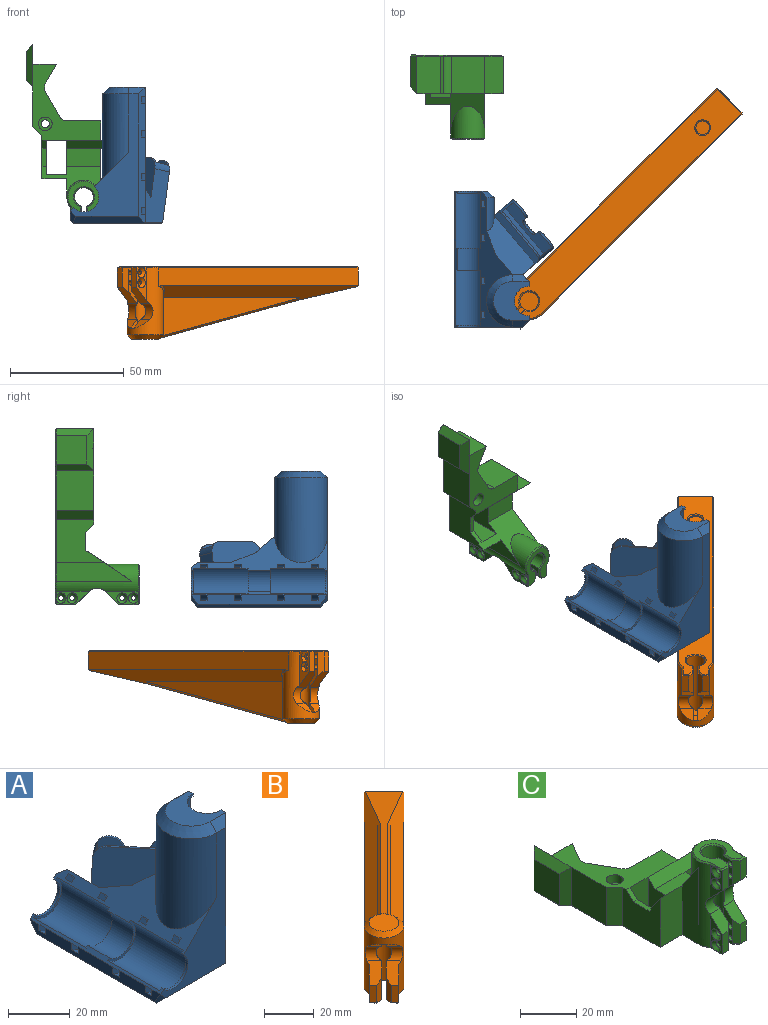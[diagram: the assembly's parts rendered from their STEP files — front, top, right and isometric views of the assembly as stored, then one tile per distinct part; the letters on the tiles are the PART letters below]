
ASSEMBLY  parts=3 mates=2
PART A: 114 faces, bbox 43.8x60x60 mm
  f0: plane 54x38.74mm, normal (0,0,-1), area 1335.7mm2, adj f1,f3,f13,f23,f24,f25,f27,f37
  f1: plane 16.85x14.14mm, normal (-0.77,-0.64,0), area 54.9mm2, adj f0,f98,f99,f100,f108,f109,f110
  f2: plane 22.93x19.76mm, normal (-0.75,-0.63,0.17), area 490.1mm2, adj f8,f81,f86,f92,f93,f94,f96
  f3: plane 11.55x8.31mm, normal (1,0,0), area 88.6mm2, adj f0,f9,f36,f81,f111
  f4: plane 24.28x21.91mm, normal (0.13,0.11,0.98), area 86.6mm2, adj f82,f83,f84,f88,f89,f90,f97
  f5: plane 60x15.09mm, normal (-0.71,0,0.71), area 433.6mm2, adj f9,f10,f11,f14,f15,f16,f17,f18
  f6: cylinder r=7.55mm len=24.1mm, axis (0,0,-1), area 571.6mm2, adj f23,f24,f31,f34
  f7: cylinder r=7.55mm len=24.1mm, axis (0,0,-1), area 571.6mm2, adj f23,f24,f28,f33
  f8: plane 0.26x0.16mm, normal (1,0,0), area 0mm2, adj f2,f9,f96
  f9: cylinder r=11.55mm len=14.54mm, axis (0,-1,0), area 110.4mm2, adj f3,f5,f8,f35,f96
  f10: cylinder r=7.55mm len=24.1mm, axis (0,-1,0), area 571.6mm2, adj f5,f12,f17,f21
  f11: cylinder r=7.55mm len=24.1mm, axis (0,-1,0), area 571.6mm2, adj f5,f12,f19,f22
  f12: plane 60x1.41mm, normal (-0.71,0,0.71), area 71.8mm2, adj f10,f11,f14,f15,f16,f17,f18,f19
  f13: plane 54x1.26mm, normal (-0.71,0,-0.71), area 96.3mm2, adj f0,f38,f39,f40
  f14: plane 14.6x14.6mm, normal (0,1,0), area 64.7mm2, adj f5,f12,f18,f35,f36,f37,f38
  f15: plane 54x30.05mm, normal (0,-1,0), area 557.1mm2, adj f5,f12,f16,f29,f40,f41,f42,f43
  f16: cylinder r=6.55mm len=11.18mm, axis (0,-1,0), area 20.6mm2, adj f5,f12,f15,f17
  f17: plane 12.89x12.89mm, normal (0,1,0), area 22.1mm2, adj f5,f10,f12,f16
  f18: cylinder r=6.55mm len=11.18mm, axis (0,1,0), area 20.6mm2, adj f5,f12,f14,f19
  f19: plane 12.89x12.89mm, normal (0,-1,0), area 22.1mm2, adj f5,f11,f12,f18
  f20: cylinder r=6.55mm len=11.18mm, axis (0,1,0), area 201.7mm2, adj f5,f12,f21,f22
  f21: plane 12.89x12.89mm, normal (0,-1,0), area 22.1mm2, adj f5,f10,f12,f20
  f22: plane 12.89x12.89mm, normal (0,1,0), area 22.1mm2, adj f5,f11,f12,f20
  f23: plane 60x2mm, normal (1,0,0), area 71.8mm2, adj f0,f6,f7,f26,f27,f28,f30,f31
  f24: plane 60x2mm, normal (1,0,0), area 71.8mm2, adj f0,f6,f7,f26,f27,f28,f30,f31
  f25: plane 57x4.28mm, normal (0,1,0), area 153.2mm2, adj f0,f29,f44,f46,f47,f86,f96,f113
  f26: plane 17.1x15.83mm, normal (0,0,1), area 172mm2, adj f23,f24,f30,f43,f45,f46
  f27: cylinder r=6.55mm len=13.1mm, axis (0,0,-1), area 20.6mm2, adj f0,f23,f24,f28
  f28: plane 15.1x7.55mm, normal (0,0,1), area 22.1mm2, adj f7,f23,f24,f27
  f29: cylinder r=11.55mm len=37.32mm, axis (0,0,1), area 1200.5mm2, adj f5,f15,f25,f45
  f30: cylinder r=6.55mm len=13.1mm, axis (0,0,1), area 20.6mm2, adj f23,f24,f26,f31
  f31: plane 15.1x7.55mm, normal (0,0,-1), area 22.1mm2, adj f6,f23,f24,f30
  f32: cylinder r=6.55mm len=13.1mm, axis (0,0,1), area 201.7mm2, adj f23,f24,f33,f34
  f33: plane 15.1x7.55mm, normal (0,0,-1), area 22.1mm2, adj f7,f23,f24,f32
  f34: plane 15.1x7.55mm, normal (0,0,1), area 22.1mm2, adj f6,f23,f24,f32
  f35: cone r=11.55mm half-angle=45deg, axis (0,-1,0), area 33.5mm2, adj f5,f9,f14,f36
  f36: plane 11.55x3mm, normal (0.71,0.71,0), area 42.6mm2, adj f3,f14,f35,f37
  f37: plane 16.33x3mm, normal (0,0.71,-0.71), area 60.3mm2, adj f0,f14,f36,f38
  f38: plane 5.5x3mm, normal (-0.5,0.71,-0.5), area 11.3mm2, adj f13,f14,f37,f39
  f39: plane 60x4.24mm, normal (-1,0,0), area 210.6mm2, adj f12,f13,f38,f40,f48,f49,f51,f52
  f40: plane 5.5x3mm, normal (-0.5,-0.71,-0.5), area 11.3mm2, adj f13,f15,f39,f41
  f41: plane 31.78x3mm, normal (0,-0.71,-0.71), area 125.8mm2, adj f0,f15,f40,f42
  f42: plane 60x3mm, normal (0.71,-0.71,0), area 210.6mm2, adj f15,f23,f41,f43,f65,f66,f67,f69
  f43: plane 7.28x3mm, normal (0,-0.71,0.71), area 24.5mm2, adj f15,f26,f42,f45
  f44: plane 60x3mm, normal (0.71,0.71,0), area 217mm2, adj f0,f24,f25,f46,f65,f66,f67,f69
  f45: cone r=8.55mm half-angle=45deg, axis (0,0,-1), area 134mm2, adj f26,f29,f43,f46
  f46: plane 7.28x3mm, normal (0,0.71,0.71), area 24.5mm2, adj f25,f26,f44,f45
  f47: plane 8.66x7.27mm, normal (0.77,0.64,0), area 41.1mm2, adj f5,f25,f96
  f48: cylinder r=10.55mm len=18.01mm, axis (0,-1,0), area 93.9mm2, adj f5,f39,f49,f51
  f49: plane 18.01x16.6mm, normal (0,-1,0), area 58.1mm2, adj f5,f39,f48,f50
  f50: cylinder r=8.55mm len=14.6mm, axis (0,-1,0), area 80.6mm2, adj f5,f12,f49,f51
  f51: plane 18.01x16.6mm, normal (0,1,0), area 58.1mm2, adj f5,f39,f48,f50
  f52: cylinder r=10.55mm len=18.01mm, axis (0,-1,0), area 93.9mm2, adj f5,f39,f53,f55
  f53: plane 18.01x16.6mm, normal (0,-1,0), area 58.1mm2, adj f5,f39,f52,f54
  f54: cylinder r=8.55mm len=14.6mm, axis (0,-1,0), area 80.6mm2, adj f5,f12,f53,f55
  f55: plane 18.01x16.6mm, normal (0,1,0), area 58.1mm2, adj f5,f39,f52,f54
  f56: cylinder r=10.55mm len=18.01mm, axis (0,1,0), area 93.9mm2, adj f5,f39,f57,f59
  f57: plane 18.01x16.6mm, normal (0,1,0), area 58.1mm2, adj f5,f39,f56,f58
  f58: cylinder r=8.55mm len=14.6mm, axis (0,1,0), area 80.6mm2, adj f5,f12,f57,f59
  f59: plane 18.01x16.6mm, normal (0,-1,0), area 58.1mm2, adj f5,f39,f56,f58
  f60: cylinder r=10.55mm len=18.01mm, axis (0,1,0), area 93.9mm2, adj f5,f39,f61,f63
  f61: plane 18.01x16.6mm, normal (0,1,0), area 58.1mm2, adj f5,f39,f60,f62
  f62: cylinder r=8.55mm len=14.6mm, axis (0,1,0), area 80.6mm2, adj f5,f12,f61,f63
  f63: plane 18.01x16.6mm, normal (0,-1,0), area 58.1mm2, adj f5,f39,f60,f62
  f64: cylinder r=8.55mm len=17.1mm, axis (0,0,1), area 80.6mm2, adj f23,f24,f65,f67
  f65: plane 20.78x10.55mm, normal (0,0,-1), area 56.2mm2, adj f42,f44,f64,f66
  f66: cylinder r=10.55mm len=20.78mm, axis (0,0,1), area 88.3mm2, adj f42,f44,f65,f67
  f67: plane 20.78x10.55mm, normal (0,0,1), area 56.2mm2, adj f42,f44,f64,f66
  f68: cylinder r=8.55mm len=17.1mm, axis (0,0,1), area 80.6mm2, adj f23,f24,f69,f71
  f69: plane 20.78x10.55mm, normal (0,0,-1), area 56.2mm2, adj f42,f44,f68,f70
  f70: cylinder r=10.55mm len=20.78mm, axis (0,0,1), area 88.3mm2, adj f42,f44,f69,f71
  f71: plane 20.78x10.55mm, normal (0,0,1), area 56.2mm2, adj f42,f44,f68,f70
  f72: cylinder r=8.55mm len=17.1mm, axis (0,0,-1), area 80.6mm2, adj f23,f24,f73,f75
  f73: plane 20.78x10.55mm, normal (0,0,1), area 56.2mm2, adj f42,f44,f72,f74
  f74: cylinder r=10.55mm len=20.78mm, axis (0,0,-1), area 88.3mm2, adj f42,f44,f73,f75
  f75: plane 20.78x10.55mm, normal (0,0,-1), area 56.2mm2, adj f42,f44,f72,f74
  f76: cylinder r=8.55mm len=17.1mm, axis (0,0,-1), area 80.6mm2, adj f23,f24,f77,f79
  f77: plane 20.78x10.55mm, normal (0,0,1), area 56.2mm2, adj f42,f44,f76,f78
  f78: cylinder r=10.55mm len=20.78mm, axis (0,0,-1), area 88.3mm2, adj f42,f44,f77,f79
  f79: plane 20.78x10.55mm, normal (0,0,-1), area 56.2mm2, adj f42,f44,f76,f78
  f80: plane 24.7x22.49mm, normal (0.75,0.63,-0.17), area 647.2mm2, adj f89,f90,f92,f93,f94,f97
  f81: plane 23.58x8.1mm, normal (-0.64,0.77,0), area 186.4mm2, adj f2,f3,f85,f93,f111
  f82: plane 7.1x5.96mm, normal (-0.64,0.77,0), area 12.1mm2, adj f0,f4,f84,f97
  f83: plane 7.1x5.96mm, normal (0.64,-0.77,0), area 12.1mm2, adj f0,f4,f84,f97
  f84: plane 13.95x11.76mm, normal (-0.75,-0.63,0.17), area 25.9mm2, adj f0,f4,f82,f83
  f85: plane 27.11x24mm, normal (0.75,0.63,-0.17), area 612.3mm2, adj f81,f86,f87,f91,f93,f94,f95,f111
  f86: plane 23.58x13.82mm, normal (0.64,-0.77,0), area 300.4mm2, adj f2,f25,f85,f94,f96,f113
  f87: plane 9.04x1.95mm, normal (-0.64,0.77,0), area 9mm2, adj f85,f88,f94,f95
  f88: plane 26.59x22.71mm, normal (-0.75,-0.63,0.17), area 549.3mm2, adj f4,f87,f89,f90,f91,f93,f94,f95
  f89: plane 25.75x8.52mm, normal (-0.64,0.77,0), area 162.7mm2, adj f4,f80,f88,f94,f97
  f90: plane 25.75x8.52mm, normal (0.64,-0.77,0), area 162.7mm2, adj f4,f80,f88,f93,f97
  f91: plane 9.04x1.95mm, normal (0.64,-0.77,0), area 9mm2, adj f85,f88,f93,f95
  f92: plane 14.42x12.32mm, normal (0.13,0.11,0.98), area 18mm2, adj f2,f80,f93,f94
  f93: cylinder r=5mm len=13.08mm, axis (-0.75,-0.63,0.17), area 44.5mm2, adj f2,f80,f81,f85,f88,f90,f91,f92
  f94: cylinder r=5mm len=13.08mm, axis (0.75,0.63,-0.17), area 44.5mm2, adj f2,f80,f85,f86,f87,f88,f89,f92
  f95: cylinder r=4mm len=6.79mm, axis (0.75,0.63,-0.17), area 12.6mm2, adj f85,f87,f88,f91
  f96: plane 26.2x21.36mm, normal (0.59,0.49,0.64), area 378.3mm2, adj f2,f5,f8,f9,f25,f47,f86
  f97: cylinder r=5mm len=23.08mm, axis (-0.64,0.77,0), area 141.4mm2, adj f0,f4,f80,f82,f83,f89,f90
  f98: plane 11.28x10.14mm, normal (0,0,-1), area 36.6mm2, adj f1,f99,f100,f105
  f99: cylinder r=5mm len=5.68mm, axis (-0.77,-0.64,0), area 20.5mm2, adj f0,f1,f98,f106
  f100: cylinder r=5mm len=5.68mm, axis (0.77,0.64,0), area 20.5mm2, adj f0,f1,f98,f104
  f101: cylinder r=2.5mm len=10.95mm, axis (-0.64,0.77,0), area 47.9mm2, adj f0,f102,f103,f107
  f102: revolved ~4.07x2.86mm, area 11.4mm2, adj f0,f101,f107
  f103: revolved ~4.18x2.73mm, area 11.4mm2, adj f0,f101,f107
  f104: revolved ~6.32x4.23mm, area 27.7mm2, adj f0,f100,f105
  f105: cylinder r=4mm len=11.92mm, axis (-0.64,0.77,0), area 76.7mm2, adj f0,f98,f104,f106
  f106: revolved ~6.21x4.36mm, area 27.7mm2, adj f0,f99,f105
  f107: plane 14.49x12.16mm, normal (0.77,0.64,0), area 19.6mm2, adj f0,f101,f102,f103,f108,f109,f110
  f108: cylinder r=2.5mm len=3.77mm, axis (0.77,0.64,0), area 8.7mm2, adj f0,f1,f107,f109
  f109: plane 11.28x10.14mm, normal (0,0,1), area 36.6mm2, adj f1,f107,f108,f110
  f110: cylinder r=2.5mm len=3.77mm, axis (0.77,0.64,0), area 8.7mm2, adj f0,f1,f107,f109
  f111: plane 5.16x4.95mm, normal (-0.45,0.54,-0.71), area 4.7mm2, adj f0,f3,f81,f85,f112
  f112: plane 21.32x18mm, normal (0.49,0.41,-0.77), area 17.6mm2, adj f0,f85,f111,f113
  f113: plane 11.61x9.14mm, normal (0.45,-0.54,-0.71), area 10.1mm2, adj f0,f25,f85,f86,f112
PART B: 90 faces, bbox 107.3x107.3x33.3 mm
  f0: cylinder r=8mm len=29.5mm, axis (0,0,-1), area 720.1mm2, adj f15,f16,f20,f24,f27,f28,f29,f50
  f1: cylinder r=4.12mm len=29.5mm, axis (0,0,-1), area 685.4mm2, adj f2,f3,f17,f21,f22,f23,f53,f54
  f2: plane 15.8x3.74mm, normal (-0.71,0.71,0), area 62.6mm2, adj f1,f4,f5,f28,f48,f53,f57
  f3: plane 15.8x3.74mm, normal (0.71,-0.71,0), area 62.6mm2, adj f1,f29,f30,f31,f49,f54,f56
  f4: cylinder r=1.05mm len=3.61mm, axis (0.71,-0.71,0), area 19.8mm2, adj f2,f47,f48
  f5: cylinder r=1.05mm len=3.61mm, axis (0.71,-0.71,0), area 19.8mm2, adj f2,f40,f48
  f6: plane 13.79x13.79mm, normal (0.71,-0.71,0), area 130.7mm2, adj f7,f11,f13,f19
  f7: plane 6.7x5.01mm, normal (1,0,0), area 33.6mm2, adj f6,f8,f13,f19
  f8: plane 6.7x3.54mm, normal (0.71,0.71,0), area 33.6mm2, adj f7,f9,f13,f19
  f9: plane 6.7x5.01mm, normal (0,1,0), area 33.6mm2, adj f8,f10,f13,f19
  f10: plane 13.79x13.79mm, normal (-0.71,0.71,0), area 130.7mm2, adj f9,f11,f13,f19
  f11: plane 10.61x10.61mm, normal (0.71,0.71,0), area 34.4mm2, adj f6,f10,f13,f19,f67,f72,f73,f77
  f12: cylinder r=3mm len=6mm, axis (0,0,-1), area 9.4mm2, adj f13,f78
  f13: plane 22.35x22.35mm, normal (0,0,1), area 238.1mm2, adj f6,f7,f8,f9,f10,f11,f12
  f14: plane 104.86x104.86mm, normal (0,0,-1), area 1872.9mm2, adj f55,f56,f57,f58,f59,f60,f61,f62
  f15: plane 88.43x88.43mm, normal (-0.71,0.71,0), area 959.3mm2, adj f0,f66,f71,f72,f84
  f16: plane 88.43x88.43mm, normal (0.71,-0.71,0), area 959.3mm2, adj f0,f68,f73,f74,f87
  f17: plane 8.25x8.25mm, normal (0,0,-1), area 53.5mm2, adj f1
  f18: plane 12x12mm, normal (0,0,1), area 113.1mm2, adj f20
  f19: plane 22.35x22.35mm, normal (0,0,-1), area 266.3mm2, adj f6,f7,f8,f9,f10,f11
  f20: cone r=6mm half-angle=45deg, axis (0,0,-1), area 113.8mm2, adj f0,f18,f79,f80,f81,f82,f85,f88
  f21: plane 4.2x4.2mm, normal (0,0,-1), area 7.7mm2, adj f1,f22,f23,f52
  f22: plane 3.94x2.78mm, normal (-0.71,0.71,0), area 7.7mm2, adj f1,f21,f51,f53
  f23: plane 3.94x2.78mm, normal (0.71,-0.71,0), area 7.7mm2, adj f1,f21,f50,f54
  f24: plane 14.5x4.24mm, normal (0.71,-0.71,0), area 41.3mm2, adj f0,f25,f28,f34,f35,f36,f37,f38
  f25: plane 8.5x2.12mm, normal (-0.71,-0.71,0), area 25.5mm2, adj f24,f28,f48,f61
  f26: plane 8.5x2.12mm, normal (-0.71,-0.71,0), area 25.5mm2, adj f27,f29,f49,f60
  f27: plane 14.5x4.24mm, normal (-0.71,0.71,0), area 36.3mm2, adj f0,f26,f29,f32,f33,f62
  f28: plane 8.62x7.8mm, normal (-0.5,-0.5,0.71), area 48.4mm2, adj f0,f2,f24,f25,f48,f53
  f29: plane 8.62x7.8mm, normal (-0.5,-0.5,0.71), area 48.4mm2, adj f0,f3,f26,f27,f49,f54
  f30: cylinder r=1.05mm len=4.14mm, axis (0.71,-0.71,0), area 24.7mm2, adj f3,f33,f49
  f31: cylinder r=1.05mm len=4.14mm, axis (0.71,-0.71,0), area 24.7mm2, adj f3,f32,f49
  f32: cone r=1.05mm half-angle=45deg, axis (-0.71,0.71,0), area 18.6mm2, adj f27,f31,f33
  f33: cone r=1.05mm half-angle=45deg, axis (-0.71,0.71,0), area 18.3mm2, adj f27,f30,f32,f62
  f34: plane 2.23x2.23mm, normal (-0.61,-0.61,-0.5), area 4.6mm2, adj f24,f35,f39,f40
  f35: plane 3.05x3.05mm, normal (0,0,-1), area 4.6mm2, adj f24,f34,f36,f40
  f36: plane 2.23x2.23mm, normal (0.61,0.61,-0.5), area 4.6mm2, adj f24,f35,f37,f40
  f37: plane 2.23x2.23mm, normal (0.61,0.61,0.5), area 4.6mm2, adj f24,f36,f38,f40
  f38: plane 3.05x3.05mm, normal (0,0,1), area 4.6mm2, adj f24,f37,f39,f40
  f39: plane 2.23x2.23mm, normal (-0.61,-0.61,0.5), area 4.6mm2, adj f24,f34,f38,f40
  f40: plane 4x3.27mm, normal (0.71,-0.71,0), area 10.4mm2, adj f5,f34,f35,f36,f37,f38,f39
  f41: plane 2.23x2.23mm, normal (-0.61,-0.61,-0.5), area 4.6mm2, adj f24,f42,f46,f47
  f42: plane 3.05x3.05mm, normal (0,0,-1), area 4.6mm2, adj f24,f41,f43,f47
  f43: plane 2.23x2.23mm, normal (0.61,0.61,-0.5), area 4.6mm2, adj f24,f42,f44,f47
  f44: plane 2.23x2.23mm, normal (0.61,0.61,0.5), area 4.6mm2, adj f24,f43,f45,f47
  f45: plane 3.05x3.05mm, normal (0,0,1), area 4.6mm2, adj f44,f46,f47,f63
  f46: plane 2.23x2.23mm, normal (-0.61,-0.61,0.5), area 4.6mm2, adj f24,f41,f45,f47
  f47: plane 4x3.27mm, normal (0.71,-0.71,0), area 10.4mm2, adj f4,f41,f42,f43,f44,f45,f46
  f48: plane 10.6x2.93mm, normal (-1,0,0), area 26.8mm2, adj f2,f4,f5,f25,f28,f59
  f49: plane 10.6x2.93mm, normal (0,-1,0), area 26.8mm2, adj f3,f26,f29,f30,f31,f58
  f50: plane 8.14x5.7mm, normal (-0.5,-0.5,-0.71), area 20.9mm2, adj f0,f23,f54
  f51: plane 8.14x5.7mm, normal (-0.5,-0.5,-0.71), area 20.9mm2, adj f0,f22,f53
  f52: plane 1.54x1.54mm, normal (-0.5,-0.5,-0.71), area 0.1mm2, adj f0,f21
  f53: cylinder r=5mm len=7.07mm, axis (-0.71,0.71,0), area 37.8mm2, adj f0,f1,f2,f22,f28,f51
  f54: cylinder r=5mm len=7.07mm, axis (0.71,-0.71,0), area 37.8mm2, adj f0,f1,f3,f23,f29,f50
  f55: cone r=4.62mm half-angle=45deg, axis (0,0,-1), area 17.7mm2, adj f1,f14,f56,f57
  f56: plane 3.96x3.85mm, normal (0.5,-0.5,-0.71), area 3.5mm2, adj f3,f14,f55,f58
  f57: plane 3.96x3.85mm, normal (-0.5,0.5,-0.71), area 3.5mm2, adj f2,f14,f55,f59
  f58: plane 2.83x0.5mm, normal (0,-0.71,-0.71), area 1.9mm2, adj f14,f49,f56,f60
  f59: plane 2.83x0.5mm, normal (-0.71,0,-0.71), area 1.9mm2, adj f14,f48,f57,f61
  f60: plane 2.33x2.12mm, normal (-0.5,-0.5,-0.71), area 1.9mm2, adj f14,f26,f58,f62
  f61: plane 2.33x2.12mm, normal (-0.5,-0.5,-0.71), area 1.9mm2, adj f14,f25,f59,f63
  f62: plane 4.74x4.25mm, normal (-0.5,0.5,-0.71), area 3.8mm2, adj f14,f27,f33,f60,f64
  f63: plane 4.74x4.25mm, normal (0.5,-0.5,-0.71), area 4.1mm2, adj f14,f24,f45,f61,f65
  f64: cone r=8mm half-angle=45deg, axis (0,0,1), area 4mm2, adj f0,f14,f62,f66
  f65: cone r=8mm half-angle=45deg, axis (0,0,1), area 4mm2, adj f0,f14,f63,f68
  f66: plane 88.39x88.39mm, normal (-0.5,0.5,-0.71), area 88mm2, adj f14,f15,f64,f69
  f67: plane 10.96x10.96mm, normal (0.5,0.5,-0.71), area 10.6mm2, adj f11,f14,f69,f70
  f68: plane 88.39x88.39mm, normal (0.5,-0.5,-0.71), area 88mm2, adj f14,f16,f65,f70
  f69: plane 0.71x0.5mm, normal (0,0.82,-0.58), area 0.2mm2, adj f66,f67,f72
  f70: plane 0.71x0.5mm, normal (0.82,0,-0.58), area 0.2mm2, adj f67,f68,f73
  f71: plane 86.82x86.46mm, normal (-0.5,0.5,0.71), area 832mm2, adj f15,f75,f80,f81,f83,f84,f88
  f72: plane 7.7x0.71mm, normal (0,1,0), area 5.4mm2, adj f11,f15,f69,f75
  f73: plane 7.7x0.71mm, normal (1,0,0), area 5.4mm2, adj f11,f16,f70,f76
  f74: plane 86.82x86.47mm, normal (0.5,-0.5,0.71), area 831.9mm2, adj f16,f76,f79,f81,f86,f87,f89
  f75: plane 0.71x0.5mm, normal (0,0.82,0.58), area 0.2mm2, adj f71,f72,f77
  f76: plane 0.71x0.5mm, normal (0.82,0,0.58), area 0.2mm2, adj f73,f74,f77
  f77: plane 10.96x10.96mm, normal (0.5,0.5,0.71), area 10.6mm2, adj f11,f75,f76,f81
  f78: cone r=3.5mm half-angle=45deg, axis (0,0,-1), area 14.4mm2, adj f12,f14
  f79: plane 61.31x61.31mm, normal (0.71,-0.71,0), area 710.6mm2, adj f20,f74,f85,f86,f89
  f80: plane 61.31x61.31mm, normal (-0.71,0.71,0), area 710.6mm2, adj f20,f71,f82,f83,f88
  f81: plane 90.27x90.27mm, normal (0.14,0.14,0.98), area 549.8mm2, adj f20,f71,f74,f77,f88,f89
  f82: plane 16.19x1.13mm, normal (-0.2,0.98,0), area 17.3mm2, adj f0,f20,f80,f83
  f83: bspline ~7.7x6.05mm, area 9.1mm2, adj f0,f71,f80,f82,f84
  f84: bspline ~2.46x1.95mm, area 1.4mm2, adj f0,f15,f71,f83
  f85: plane 16.19x1.13mm, normal (0.98,-0.2,0), area 17.3mm2, adj f0,f20,f79,f86
  f86: bspline ~7.7x6.05mm, area 9.1mm2, adj f0,f74,f79,f85,f87
  f87: bspline ~2.46x1.95mm, area 1.4mm2, adj f0,f16,f74,f86
  f88: plane 62.71x62.1mm, normal (-0.4,0.6,0.69), area 125.6mm2, adj f20,f71,f80,f81
  f89: plane 62.71x62.1mm, normal (0.6,-0.4,0.69), area 125.6mm2, adj f20,f74,f79,f81
PART C: 146 faces, bbox 41x77.7x37 mm
  f0: plane 33.25x21.5mm, normal (1,0,0), area 416.2mm2, adj f11,f29,f32,f89,f129
  f1: cylinder r=1.05mm len=3mm, axis (1,0,0), area 19.8mm2, adj f41,f81,f96
  f2: cylinder r=1.05mm len=3mm, axis (1,0,0), area 19.8mm2, adj f41,f74,f96
  f3: cylinder r=1.05mm len=3mm, axis (1,0,0), area 19.8mm2, adj f8,f67,f94
  f4: cylinder r=1.05mm len=3mm, axis (1,0,0), area 19.8mm2, adj f8,f60,f94
  f5: plane 8.5x3mm, normal (0,-1,0), area 25.5mm2, adj f9,f48,f95,f111
  f6: plane 8.5x3mm, normal (0,-1,0), area 25.5mm2, adj f45,f46,f96,f138
  f7: plane 15.09x4.5mm, normal (1,0,0), area 50.5mm2, adj f39,f48,f51,f54,f55,f95,f115
  f8: plane 15.09x4.5mm, normal (-1,0,0), area 50.5mm2, adj f3,f4,f39,f47,f50,f94,f119
  f9: plane 14.5x6mm, normal (-1,0,0), area 36.2mm2, adj f5,f11,f48,f51,f56,f57,f109
  f10: plane 14.5x6mm, normal (1,0,0), area 41.3mm2, adj f11,f44,f47,f50,f61,f63,f64,f65
  f11: cylinder r=7.5mm len=36mm, axis (0,0,-1), area 564.8mm2, adj f0,f9,f10,f28,f32,f42,f45,f50
  f12: plane 75.96x39.29mm, normal (0,0,-1), area 837.9mm2, adj f100,f101,f102,f103,f104,f105,f106,f107
  f13: plane 18.25x15mm, normal (-1,0,0), area 210.3mm2, adj f14,f29,f31,f32,f36,f134
  f14: plane 16.5x9mm, normal (0,-1,0), area 148.5mm2, adj f13,f24,f33,f132
  f15: cylinder r=1.75mm len=13mm, axis (0,0,-1), area 142.9mm2, adj f16,f135
  f16: plane 6x6mm, normal (0,0,1), area 18.7mm2, adj f15,f22
  f17: plane 16.5x8.5mm, normal (1,0,0), area 140.2mm2, adj f18,f24,f88,f124
  f18: plane 16.5x14.69mm, normal (0,1,0), area 242.3mm2, adj f17,f24,f26,f122
  f19: plane 16.5x10.72mm, normal (0.87,0.5,0), area 204.2mm2, adj f24,f26,f27,f118
  f20: plane 16.5x8.28mm, normal (0.87,-0.5,0), area 157.8mm2, adj f21,f24,f27,f114
  f21: plane 16.5x10.44mm, normal (0,1,0), area 172.2mm2, adj f20,f24,f90,f112
  f22: cylinder r=3mm len=6mm, axis (0,0,-1), area 66mm2, adj f16,f24
  f23: plane 17.5x16.5mm, normal (-1,0,0), area 288.8mm2, adj f24,f25,f93,f102
  f24: plane 33.5x30mm, normal (0,0,1), area 418.1mm2, adj f14,f17,f18,f19,f20,f21,f22,f23
  f25: plane 16.5x4mm, normal (-0.71,-0.71,0), area 93.3mm2, adj f23,f24,f34,f100
  f26: cylinder r=4mm len=16.5mm, axis (0,0,1), area 69.1mm2, adj f18,f19,f24,f120
  f27: cylinder r=4mm len=16.5mm, axis (0,0,1), area 69.1mm2, adj f19,f20,f24,f116
  f28: plane 33.25x8mm, normal (-1,0,0), area 218mm2, adj f11,f32,f35,f105
  f29: plane 15x8mm, normal (0,0,1), area 120mm2, adj f0,f13,f31,f32
  f30: plane 17x14mm, normal (0,0,1), area 109.3mm2, adj f136,f137,f138,f139,f140,f141,f142,f143
  f31: plane 23x3.5mm, normal (0,-0.71,0.71), area 105.2mm2, adj f13,f24,f29,f88,f89,f98
  f32: plane 26x20.25mm, normal (0,0.83,0.55), area 258.1mm2, adj f0,f11,f13,f28,f29,f33,f34,f35
  f33: plane 18.25x15mm, normal (1,0,0), area 210.3mm2, adj f14,f32,f36,f37,f38,f131
  f34: plane 21.25x19mm, normal (-1,0,0), area 282.8mm2, adj f24,f25,f32,f35,f37,f38,f101
  f35: plane 21.25x11mm, normal (0,-1,0), area 233.7mm2, adj f28,f32,f34,f103
  f36: plane 18.25x9mm, normal (0,1,0), area 164.2mm2, adj f13,f32,f33,f133
  f37: plane 8x2mm, normal (0,0,1), area 16mm2, adj f32,f33,f34,f38
  f38: plane 3.5x3.5mm, normal (0,-0.71,0.71), area 9.9mm2, adj f24,f33,f34,f37
  f39: cylinder r=4.12mm len=36mm, axis (0,0,1), area 843.2mm2, adj f7,f8,f40,f41,f50,f51,f117,f143
  f40: plane 15.09x4.5mm, normal (1,0,0), area 50.5mm2, adj f39,f49,f51,f52,f53,f97,f145
  f41: plane 15.09x4.5mm, normal (-1,0,0), area 50.5mm2, adj f1,f2,f39,f46,f50,f96,f141
  f42: plane 14.5x6mm, normal (-1,0,0), area 36.2mm2, adj f11,f43,f49,f51,f58,f59,f140
  f43: plane 8.5x3mm, normal (0,-1,0), area 25.5mm2, adj f42,f49,f97,f142
  f44: plane 8.5x3mm, normal (0,-1,0), area 25.5mm2, adj f10,f47,f94,f123
  f45: plane 14.5x6mm, normal (1,0,0), area 41.3mm2, adj f6,f11,f46,f50,f75,f76,f77,f78
  f46: plane 5.96x5.96mm, normal (0,-0.71,-0.71), area 39.3mm2, adj f6,f41,f45,f50,f96
  f47: plane 5.96x5.96mm, normal (0,-0.71,0.71), area 39.3mm2, adj f8,f10,f44,f50,f94
  f48: plane 5.96x5.96mm, normal (0,-0.71,0.71), area 39.3mm2, adj f5,f7,f9,f51,f95
  f49: plane 5.96x5.96mm, normal (0,-0.71,-0.71), area 39.3mm2, adj f40,f42,f43,f51,f97
  f50: cylinder r=5mm len=7.07mm, axis (-1,0,0), area 35.8mm2, adj f8,f10,f11,f39,f41,f45,f46,f47
  f51: cylinder r=5mm len=7.07mm, axis (-1,0,0), area 35.8mm2, adj f7,f9,f11,f39,f40,f42,f48,f49
  f52: cylinder r=1.05mm len=3.75mm, axis (1,0,0), area 24.7mm2, adj f40,f58,f97
  f53: cylinder r=1.05mm len=3.75mm, axis (1,0,0), area 24.7mm2, adj f40,f59,f97
  f54: cylinder r=1.05mm len=3.75mm, axis (1,0,0), area 24.7mm2, adj f7,f57,f95
  f55: cylinder r=1.05mm len=3.75mm, axis (1,0,0), area 24.7mm2, adj f7,f56,f95
  f56: cone r=2.3mm half-angle=45deg, axis (-1,0,0), area 18.3mm2, adj f9,f55,f109
  f57: cone r=2.3mm half-angle=45deg, axis (-1,0,0), area 18.6mm2, adj f9,f54
  f58: cone r=2.3mm half-angle=45deg, axis (-1,0,0), area 18.6mm2, adj f42,f52
  f59: cone r=2.3mm half-angle=45deg, axis (-1,0,0), area 18.3mm2, adj f42,f53,f140
  f60: plane 4.62x4mm, normal (1,0,0), area 10.4mm2, adj f4,f61,f62,f63,f64,f65,f66
  f61: plane 2x2mm, normal (0,0.87,0.5), area 4.6mm2, adj f10,f60,f62,f66
  f62: plane 2.31x2mm, normal (0,0,1), area 4.6mm2, adj f60,f61,f63,f125
  f63: plane 2x2mm, normal (0,-0.87,0.5), area 4.6mm2, adj f10,f60,f62,f64
  f64: plane 2x2mm, normal (0,-0.87,-0.5), area 4.6mm2, adj f10,f60,f63,f65
  f65: plane 2.31x2mm, normal (0,0,-1), area 4.6mm2, adj f10,f60,f64,f66
  f66: plane 2x2mm, normal (0,0.87,-0.5), area 4.6mm2, adj f10,f60,f61,f65
  f67: plane 4.62x4mm, normal (1,0,0), area 10.4mm2, adj f3,f68,f69,f70,f71,f72,f73
  f68: plane 2x2mm, normal (0,0.87,0.5), area 4.6mm2, adj f10,f67,f69,f73
  f69: plane 2.31x2mm, normal (0,0,1), area 4.6mm2, adj f10,f67,f68,f70
  f70: plane 2x2mm, normal (0,-0.87,0.5), area 4.6mm2, adj f10,f67,f69,f71
  f71: plane 2x2mm, normal (0,-0.87,-0.5), area 4.6mm2, adj f10,f67,f70,f72
  f72: plane 2.31x2mm, normal (0,0,-1), area 4.6mm2, adj f10,f67,f71,f73
  f73: plane 2x2mm, normal (0,0.87,-0.5), area 4.6mm2, adj f10,f67,f68,f72
  f74: plane 4.62x4mm, normal (1,0,0), area 10.4mm2, adj f2,f75,f76,f77,f78,f79,f80
  f75: plane 2x2mm, normal (0,0.87,0.5), area 4.6mm2, adj f45,f74,f76,f80
  f76: plane 2.31x2mm, normal (0,0,1), area 4.6mm2, adj f45,f74,f75,f77
  f77: plane 2x2mm, normal (0,-0.87,0.5), area 4.6mm2, adj f45,f74,f76,f78
  f78: plane 2x2mm, normal (0,-0.87,-0.5), area 4.6mm2, adj f45,f74,f77,f79
  f79: plane 2.31x2mm, normal (0,0,-1), area 4.6mm2, adj f74,f78,f80,f137
  f80: plane 2x2mm, normal (0,0.87,-0.5), area 4.6mm2, adj f45,f74,f75,f79
  f81: plane 4.62x4mm, normal (1,0,0), area 10.4mm2, adj f1,f82,f83,f84,f85,f86,f87
  f82: plane 2x2mm, normal (0,0.87,0.5), area 4.6mm2, adj f45,f81,f83,f87
  f83: plane 2.31x2mm, normal (0,0,1), area 4.6mm2, adj f45,f81,f82,f84
  f84: plane 2x2mm, normal (0,-0.87,0.5), area 4.6mm2, adj f45,f81,f83,f85
  f85: plane 2x2mm, normal (0,-0.87,-0.5), area 4.6mm2, adj f45,f81,f84,f86
  f86: plane 2.31x2mm, normal (0,0,-1), area 4.6mm2, adj f45,f81,f85,f87
  f87: plane 2x2mm, normal (0,0.87,-0.5), area 4.6mm2, adj f45,f81,f82,f86
  f88: plane 16.5x8mm, normal (0,1,0), area 132mm2, adj f17,f31,f98,f126
  f89: plane 13x4.5mm, normal (0,-1,0), area 58.5mm2, adj f0,f31,f98,f130
  f90: plane 16.5x8.67mm, normal (1,0,0), area 143mm2, adj f21,f92,f99,f110
  f91: plane 13.5x12.67mm, normal (-1,0,0), area 171mm2, adj f92,f93,f99,f106
  f92: plane 16.5x3mm, normal (-0.71,0.71,0), area 63.6mm2, adj f90,f91,f99,f108
  f93: plane 16.5x3mm, normal (-0.71,-0.71,0), area 63.6mm2, adj f23,f91,f99,f104
  f94: plane 10.5x2mm, normal (-0.71,-0.71,0), area 26.8mm2, adj f3,f4,f8,f44,f47,f121
  f95: plane 10.5x2mm, normal (0.71,-0.71,0), area 26.8mm2, adj f5,f7,f48,f54,f55,f113
  f96: plane 10.5x2mm, normal (-0.71,-0.71,0), area 26.8mm2, adj f1,f2,f6,f41,f46,f139
  f97: plane 10.5x2mm, normal (0.71,-0.71,0), area 26.8mm2, adj f40,f43,f49,f52,f53,f144
  f98: plane 16.5x3.5mm, normal (0.71,-0.71,0), area 73mm2, adj f31,f88,f89,f128
  f99: plane 18.67x3mm, normal (-0.71,0,0.71), area 66.5mm2, adj f24,f90,f91,f92,f93
  f100: plane 4.5x4.21mm, normal (-0.5,-0.5,-0.71), area 4mm2, adj f12,f25,f101,f102
  f101: plane 19.21x0.5mm, normal (-0.71,0,-0.71), area 13.3mm2, adj f12,f34,f100,f103
  f102: plane 17.71x0.5mm, normal (-0.71,0,-0.71), area 12.4mm2, adj f12,f23,f100,f104
  f103: plane 11.5x0.5mm, normal (0,-0.71,-0.71), area 7.8mm2, adj f12,f35,f101,f105
  f104: plane 3.5x3.21mm, normal (-0.5,-0.5,-0.71), area 3mm2, adj f12,f93,f102,f106
  f105: plane 8.5x0.5mm, normal (-0.71,0,-0.71), area 5.8mm2, adj f12,f28,f103,f107
  f106: plane 12.67x0.5mm, normal (-0.71,0,-0.71), area 8.8mm2, adj f12,f91,f104,f108
  f107: cone r=7.5mm half-angle=45deg, axis (0,0,1), area 3.4mm2, adj f11,f12,f105,f109
  f108: plane 3.21x3mm, normal (-0.5,0.5,-0.71), area 2.5mm2, adj f12,f92,f106,f110
  f109: plane 6.17x0.5mm, normal (-0.71,0,-0.71), area 3.8mm2, adj f9,f12,f56,f107,f111
  f110: plane 9.17x0.5mm, normal (0.71,0,-0.71), area 5.9mm2, adj f12,f90,f108,f112
  f111: plane 3x0.5mm, normal (0,-0.71,-0.71), area 1.9mm2, adj f5,f12,f109,f113
  f112: plane 10.94x0.5mm, normal (0,0.71,-0.71), area 7.3mm2, adj f12,f21,f110,f114
  f113: plane 2.21x2.21mm, normal (0.5,-0.5,-0.71), area 1.9mm2, adj f12,f95,f111,f115
  f114: plane 8.28x5.21mm, normal (0.61,-0.35,-0.71), area 6.5mm2, adj f12,f20,f112,f116
  f115: plane 4.52x0.52mm, normal (0.71,0,-0.71), area 3mm2, adj f7,f12,f113,f117
  f116: cone r=4.5mm half-angle=45deg, axis (0,0,-1), area 3.1mm2, adj f12,f27,f114,f118
  f117: cone r=4.12mm half-angle=45deg, axis (0,0,-1), area 17.7mm2, adj f12,f39,f115,f119
  f118: plane 10.97x6.62mm, normal (0.61,0.35,-0.71), area 8.8mm2, adj f12,f19,f116,f120
  f119: plane 4.52x0.52mm, normal (-0.71,0,-0.71), area 3mm2, adj f8,f12,f117,f121
  f120: cone r=4.5mm half-angle=45deg, axis (0,0,-1), area 3.1mm2, adj f12,f26,f118,f122
  f121: plane 2.21x2.21mm, normal (-0.5,-0.5,-0.71), area 1.9mm2, adj f12,f94,f119,f123
  f122: plane 14.69x0.5mm, normal (0,0.71,-0.71), area 10.2mm2, adj f12,f18,f120,f124
  f123: plane 3x0.5mm, normal (0,-0.71,-0.71), area 1.9mm2, adj f12,f44,f121,f125
  f124: plane 9x0.5mm, normal (0.71,0,-0.71), area 6mm2, adj f12,f17,f122,f126
  f125: plane 6.17x0.5mm, normal (0.71,0,-0.71), area 4.1mm2, adj f10,f12,f62,f123,f127
  f126: plane 8.5x0.5mm, normal (0,0.71,-0.71), area 5.4mm2, adj f12,f88,f124,f128
  f127: cone r=7.5mm half-angle=45deg, axis (0,0,1), area 3.4mm2, adj f11,f12,f125,f129
  f128: plane 3.71x3.5mm, normal (0.5,-0.5,-0.71), area 3mm2, adj f12,f98,f126,f130
  f129: plane 22x0.5mm, normal (0.71,0,-0.71), area 15.4mm2, adj f0,f12,f127,f130
  f130: plane 5x0.5mm, normal (0,-0.71,-0.71), area 3.3mm2, adj f12,f89,f128,f129
  f131: plane 16x0.5mm, normal (0.71,0,-0.71), area 11mm2, adj f12,f33,f132,f133
  f132: plane 10x0.5mm, normal (0,-0.71,-0.71), area 6.7mm2, adj f12,f14,f131,f134
  f133: plane 10x0.5mm, normal (0,0.71,-0.71), area 6.7mm2, adj f12,f36,f131,f134
  f134: plane 16x0.5mm, normal (-0.71,0,-0.71), area 11mm2, adj f12,f13,f132,f133
  f135: cone r=2.25mm half-angle=45deg, axis (0,0,-1), area 8.9mm2, adj f12,f15
  f136: cone r=7mm half-angle=45deg, axis (0,0,-1), area 22.8mm2, adj f11,f30,f137,f140
  f137: plane 6.17x0.5mm, normal (0.71,0,0.71), area 4.1mm2, adj f30,f45,f79,f136,f138
  f138: plane 3x0.5mm, normal (0,-0.71,0.71), area 1.9mm2, adj f6,f30,f137,f139
  f139: plane 2.21x2.21mm, normal (-0.5,-0.5,0.71), area 1.9mm2, adj f30,f96,f138,f141
  f140: plane 6.17x0.5mm, normal (-0.71,0,0.71), area 3.8mm2, adj f30,f42,f59,f136,f142
  f141: plane 4.52x0.52mm, normal (-0.71,0,0.71), area 3mm2, adj f30,f41,f139,f143
  f142: plane 3x0.5mm, normal (0,-0.71,0.71), area 1.9mm2, adj f30,f43,f140,f144
  f143: cone r=4.12mm half-angle=45deg, axis (0,0,1), area 17.7mm2, adj f30,f39,f141,f145
  f144: plane 2.21x2.21mm, normal (0.5,-0.5,0.71), area 1.9mm2, adj f30,f97,f142,f145
  f145: plane 4.52x0.52mm, normal (0.71,0,0.71), area 3mm2, adj f30,f40,f143,f144
PLACE A rot(axis=(0.02,1,0),0deg) t=(-76.37,-87.92,19.66)mm
PLACE B rot(axis=(0.71,0.71,0),180deg) t=(94.12,116.11,0.5)mm
PLACE C rot(axis=(1,0,0),90deg) t=(-125.87,31.9,56.21)mm
MATE slider A.f27 <-> B.f0  axis (0,0,-1) through (-76.37,-76.37,19.66)mm
MATE slider A.f9 <-> C.f11  axis (0,1,0) through (-103.37,-27.92,31.21)mm
